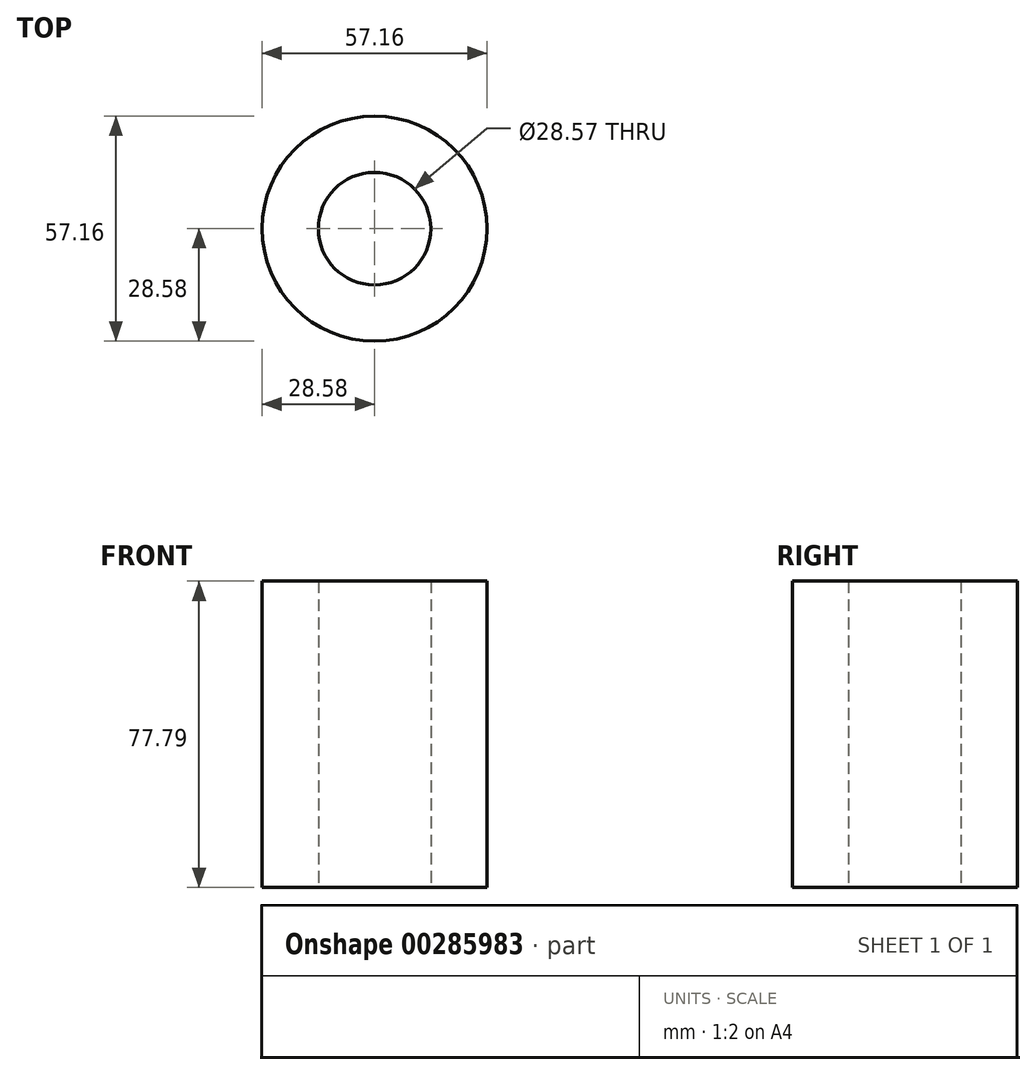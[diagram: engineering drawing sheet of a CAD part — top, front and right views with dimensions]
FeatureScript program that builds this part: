
annotation { "Feature Type Name" : "Feature", "Feature Type Description" : "" }
export const myFeature = defineFeature(function(context is Context, id is Id, definition is map)
    precondition{}
    {
        {
            var Q0;
            Q0=qCreatedBy(makeId("Top.planeOp"),FACE);
            var sketch = newSketch(context, id + "F0", { "sketchPlane" : qUnion([Q0])});
            skCircle(sketch, "E0", {"center": v(0, 0) * mm, "radius": 14.29 * mm});
            skCircle(sketch, "E1", {"center": v(0, 0) * mm, "radius": 28.58 * mm});
            skSolve(sketch);
        }
        {
            var Q0;
            Q0 = qSketchRegion(id + "F0", true);
            extrude(context, id + "F1", {"entities" : qUnion([Q0]), "depth" : 77.8 * mm});
        }
    });
